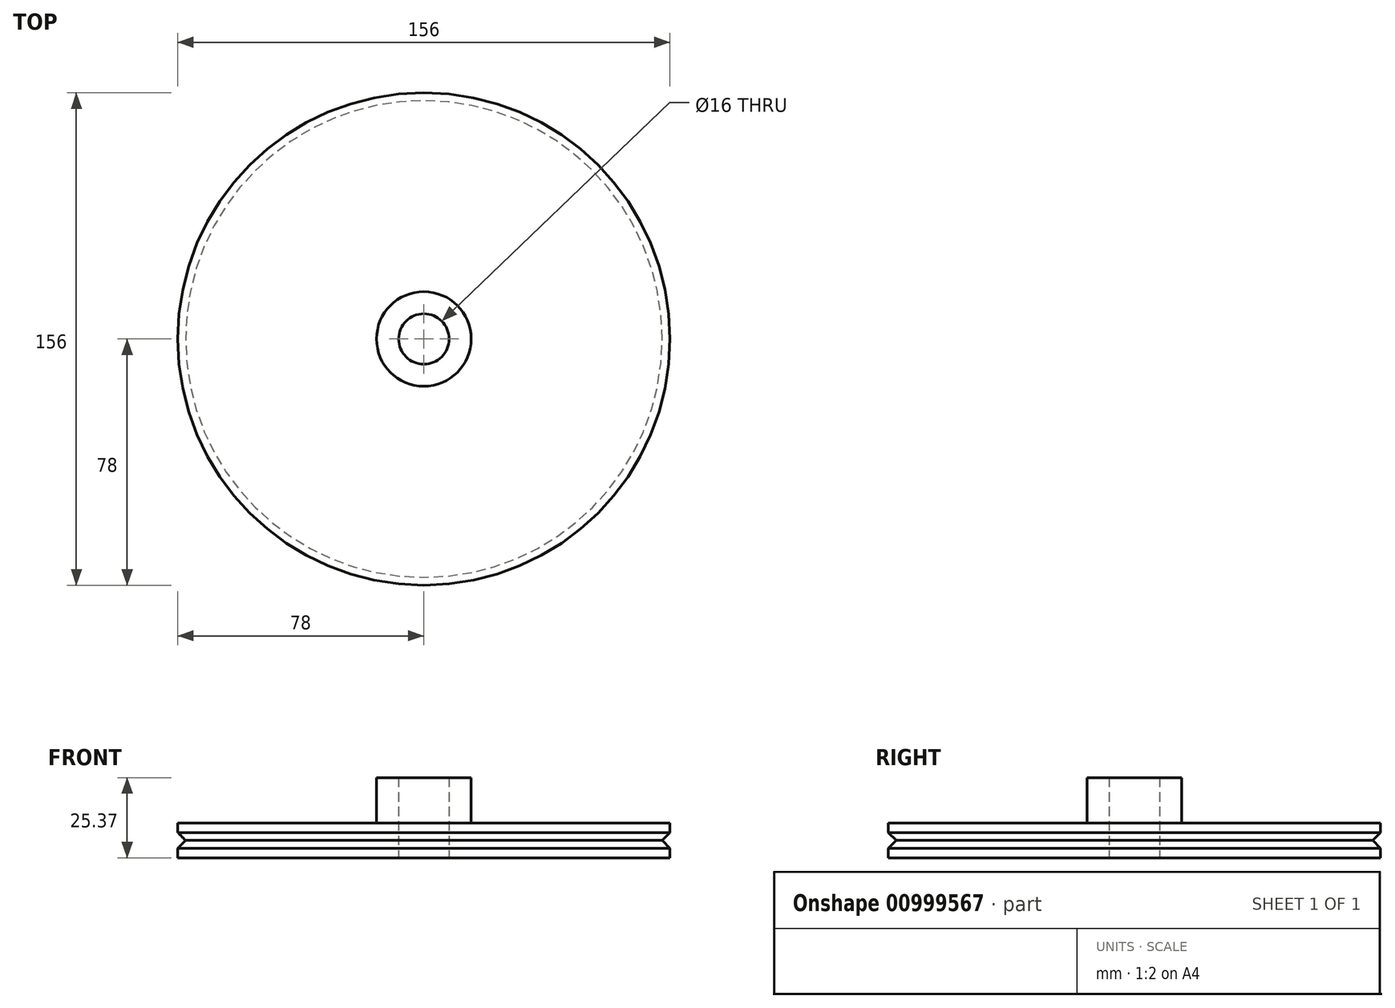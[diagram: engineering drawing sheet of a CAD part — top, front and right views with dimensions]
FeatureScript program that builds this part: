
annotation { "Feature Type Name" : "Feature", "Feature Type Description" : "" }
export const myFeature = defineFeature(function(context is Context, id is Id, definition is map)
    precondition{}
    {
        {
            var Q0;
            Q0=qCreatedBy(makeId("Front.planeOp"),FACE);
            var sketch = newSketch(context, id + "F0", { "sketchPlane" : qUnion([Q0])});
            skLineSegment(sketch, "E0", {"start": v(8, 0) * mm, "end": v(78, 0) * mm});
            skLineSegment(sketch, "E1", {"start": v(78, 0) * mm, "end": v(78, 3) * mm});
            skLineSegment(sketch, "E2", {"start": v(78, 3) * mm, "end": v(75.5, 5.5) * mm});
            skLineSegment(sketch, "E3", {"start": v(78, 11) * mm, "end": v(15, 11) * mm});
            skLineSegment(sketch, "E4", {"start": v(15, 11) * mm, "end": v(15, 25.37) * mm});
            skLineSegment(sketch, "E5", {"start": v(8, 25.37) * mm, "end": v(8, 0) * mm});
            skLineSegment(sketch, "E6", {"start": v(75.5, 5.5) * mm, "end": v(78, 8) * mm});
            skLineSegment(sketch, "E7", {"start": v(78, 11) * mm, "end": v(78, 8) * mm});
            skLineSegment(sketch, "E8", {"start": v(8, 25.37) * mm, "end": v(15, 25.37) * mm});
            skLineSegment(sketch, "E9", {"start": v(0, 0) * mm, "end": v(0, 35.71) * mm});
            skSolve(sketch);
        }
        {
            var Q0;
            Q0=makeQuery(id+"F0.imprint","IMPRINT",FACE,{"disambiguationData":[TD([[makeQuery(id+"F0.imprint","IMPRINT",EDGE,{"derivedFrom":sQuery(id+"F0.wireOp",EDGE,"E0")}),1.0]])]});
            var Q1;
            Q1=sQuery(id+"F0.wireOp",EDGE,"E9");
            revolve(context, id + "F1", {"surfaceOperationType" : NewSurfaceOperationType.NEW, "entities" : qUnion([Q0]), "axis" : qUnion([Q1]), "revolveType" : RevolveType.FULL});
        }
    });
